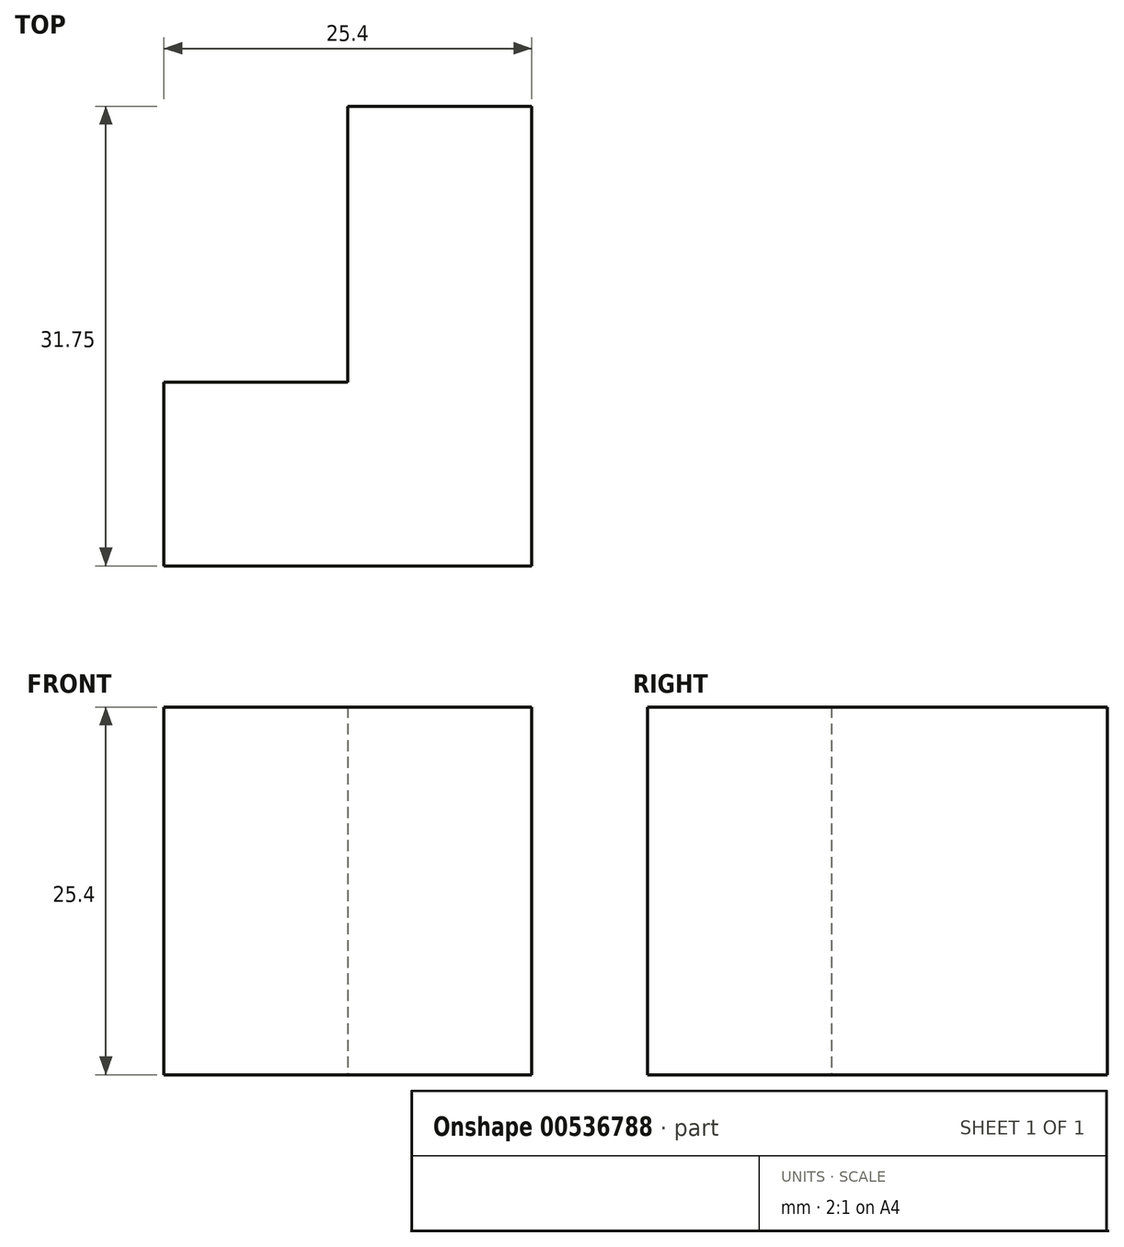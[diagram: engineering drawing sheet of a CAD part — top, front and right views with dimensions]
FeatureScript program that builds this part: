
annotation { "Feature Type Name" : "Feature", "Feature Type Description" : "" }
export const myFeature = defineFeature(function(context is Context, id is Id, definition is map)
    precondition{}
    {
        {
            var Q0;
            Q0=qCreatedBy(makeId("Top.planeOp"),FACE);
            var sketch = newSketch(context, id + "F0", { "sketchPlane" : qUnion([Q0])});
            skLineSegment(sketch, "E0", {"start": v(0, 0) * mm, "end": v(12.7, 0) * mm});
            skLineSegment(sketch, "E1", {"start": v(12.7, 0) * mm, "end": v(12.7, -31.75) * mm});
            skLineSegment(sketch, "E2", {"start": v(12.7, -31.75) * mm, "end": v(-12.7, -31.75) * mm});
            skLineSegment(sketch, "E3", {"start": v(-12.7, -31.75) * mm, "end": v(-12.7, -19.05) * mm});
            skLineSegment(sketch, "E4", {"start": v(-12.7, -19.05) * mm, "end": v(0, -19.05) * mm});
            skLineSegment(sketch, "E5", {"start": v(0, -19.05) * mm, "end": v(0, 0) * mm});
            skSolve(sketch);
        }
        {
            var Q0;
            Q0 = qSketchRegion(id + "F0", true);
            extrude(context, id + "F1", {"entities" : qUnion([Q0]), "depth" : 25.4 * mm, "offsetDistance" : 25.4 * mm});
        }
    });
